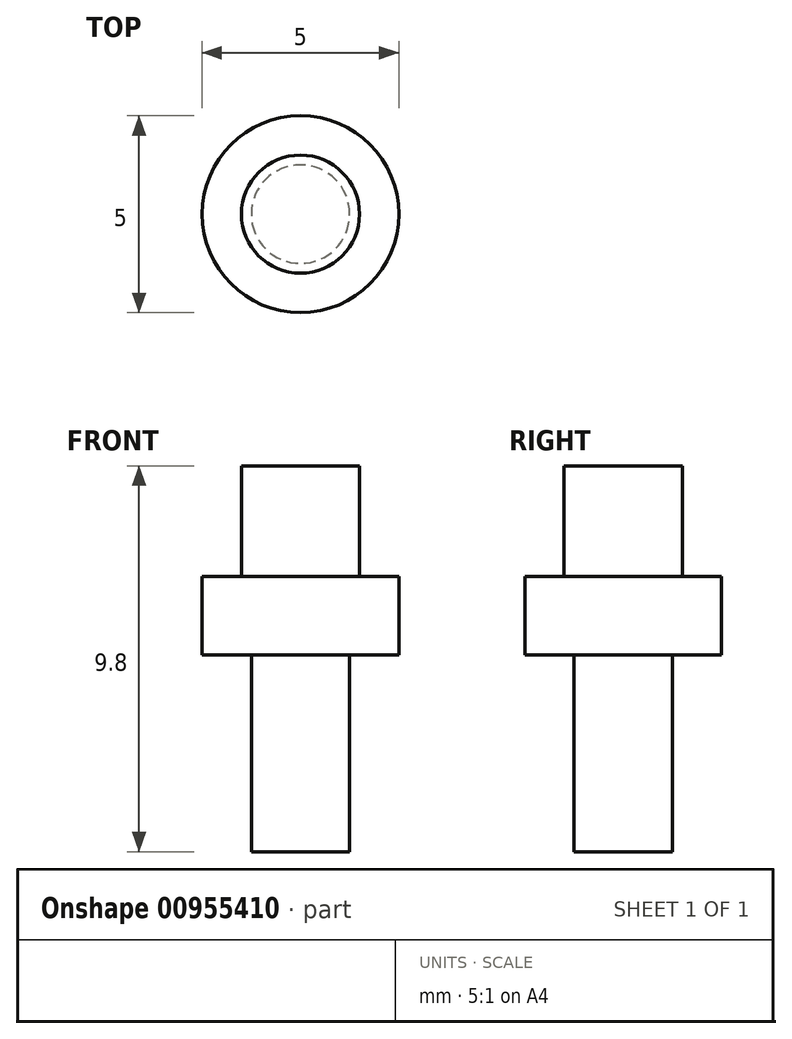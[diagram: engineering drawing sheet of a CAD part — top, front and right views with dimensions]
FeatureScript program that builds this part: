
annotation { "Feature Type Name" : "Feature", "Feature Type Description" : "" }
export const myFeature = defineFeature(function(context is Context, id is Id, definition is map)
    precondition{}
    {
        {
            var Q0;
            Q0=qCreatedBy(makeId("Top.planeOp"),FACE);
            var sketch = newSketch(context, id + "F0", { "sketchPlane" : qUnion([Q0])});
            skCircle(sketch, "E0", {"center": v(0, 0) * mm, "radius": 1.5 * mm});
            skSolve(sketch);
        }
        {
            var Q0;
            Q0 = qSketchRegion(id + "F0", true);
            extrude(context, id + "F1", {"entities" : qUnion([Q0]), "depth" : 2.8 * mm, "offsetDistance" : 25 * mm});
        }
        {
            var Q0;
            Q0=makeQuery(id+"F1.opExtrude","CAP_FACE",FACE,{"disambiguationData":[OSD([sQuery(id+"F0.wireOp",EDGE,"E0")])],"isStart":true});
            var sketch = newSketch(context, id + "F2", { "sketchPlane" : qUnion([Q0])});
            skCircle(sketch, "E1", {"center": v(0, 0) * mm, "radius": 2.5 * mm});
            skSolve(sketch);
        }
        {
            var Q0;
            Q0=makeQuery(id+"F2.imprint","IMPRINT",FACE,{"disambiguationData":[TD([[makeQuery(id+"F2.imprint","IMPRINT",EDGE,{"derivedFrom":sQuery(id+"F2.wireOp",EDGE,"E1")}),1.0]])]});
            var Q1;
            Q1=makeQuery(id+"F2.imprint","IMPRINT",FACE,{"disambiguationData":[TD([[makeQuery(id+"F2.imprint","IMPRINT",EDGE,{"derivedFrom":makeQuery(id+"F1.opExtrude","CAP_EDGE",EDGE,{"disambiguationData":[OSD([sQuery(id+"F0.wireOp",EDGE,"E0")])],"isStart":true})}),-1.0]])]});
            extrude(context, id + "F3", {"entities" : qUnion([Q0, Q1]), "operationType" : NewBodyOperationType.ADD, "depth" : 2 * mm, "offsetDistance" : 25 * mm});
        }
        {
            var Q0;
            Q0=makeQuery(id+"F3.opExtrude","CAP_FACE",FACE,{"disambiguationData":[OSD([sQuery(id+"F2.wireOp",EDGE,"E1")])],"isStart":false});
            var sketch = newSketch(context, id + "F4", { "sketchPlane" : qUnion([Q0])});
            skCircle(sketch, "E2", {"center": v(0, 0) * mm, "radius": 1.25 * mm});
            skSolve(sketch);
        }
        {
            var Q0;
            Q0 = qSketchRegion(id + "F4", true);
            extrude(context, id + "F5", {"entities" : qUnion([Q0]), "operationType" : NewBodyOperationType.ADD, "depth" : 5 * mm, "offsetDistance" : 25 * mm});
        }
    });
